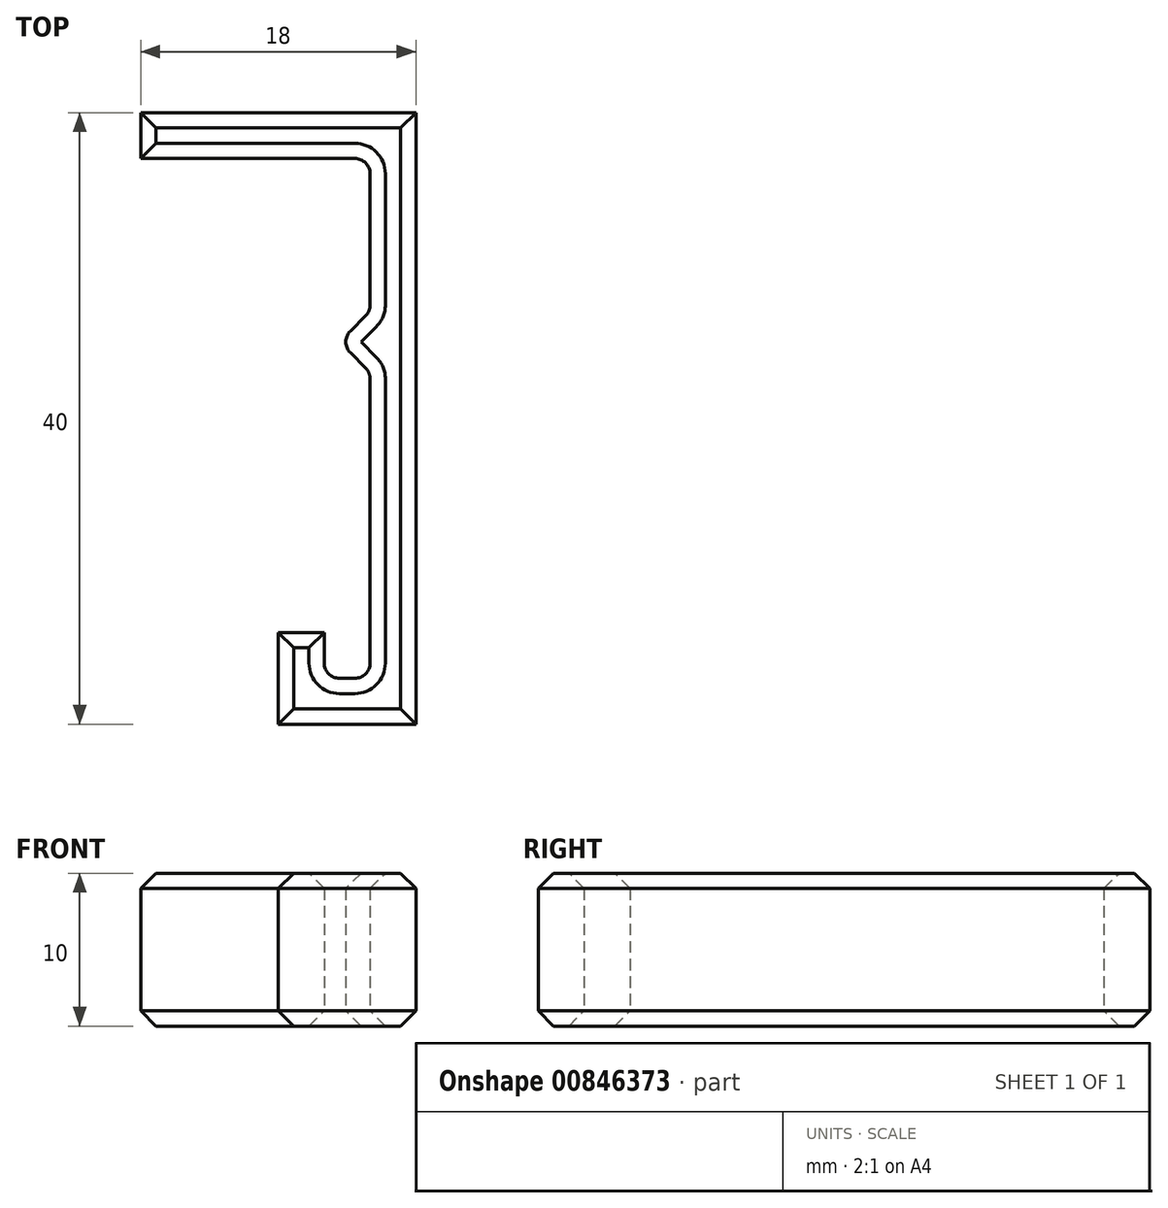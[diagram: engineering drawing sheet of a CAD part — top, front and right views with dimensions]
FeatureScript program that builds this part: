
annotation { "Feature Type Name" : "Feature", "Feature Type Description" : "" }
export const myFeature = defineFeature(function(context is Context, id is Id, definition is map)
    precondition{}
    {
        {
            var Q0;
            Q0=qCreatedBy(makeId("Top.planeOp"),FACE);
            var sketch = newSketch(context, id + "F0", { "sketchPlane" : qUnion([Q0])});
            skLineSegment(sketch, "E0", {"start": v(0, 0) * mm, "end": v(0, -3) * mm});
            skLineSegment(sketch, "E1", {"start": v(0, -3) * mm, "end": v(15, -3) * mm});
            skLineSegment(sketch, "E2", {"start": v(15, -3) * mm, "end": v(15, -13) * mm});
            skLineSegment(sketch, "E3", {"start": v(15, -13) * mm, "end": v(13, -15) * mm});
            skLineSegment(sketch, "E4", {"start": v(13, -15) * mm, "end": v(15, -17) * mm});
            skLineSegment(sketch, "E5", {"start": v(15, -17) * mm, "end": v(15, -37) * mm});
            skLineSegment(sketch, "E6", {"start": v(0, 0) * mm, "end": v(18, 0) * mm});
            skLineSegment(sketch, "E7", {"start": v(18, 0) * mm, "end": v(18, -40) * mm});
            skLineSegment(sketch, "E8", {"start": v(18, -40) * mm, "end": v(9, -40) * mm});
            skLineSegment(sketch, "E9", {"start": v(9, -40) * mm, "end": v(9, -34) * mm});
            skLineSegment(sketch, "E10", {"start": v(9, -34) * mm, "end": v(12, -34) * mm});
            skLineSegment(sketch, "E11", {"start": v(12, -34) * mm, "end": v(12, -37) * mm});
            skLineSegment(sketch, "E12", {"start": v(12, -37) * mm, "end": v(15, -37) * mm});
            skSolve(sketch);
        }
        {
            var Q0;
            Q0 = qSketchRegion(id + "F0", true);
            extrude(context, id + "F1", {"entities" : qUnion([Q0]), "depth" : 10 * mm, "offsetDistance" : 25 * mm});
        }
        {
            var Q0;
            Q0=makeQuery(id+"F1.opExtrude","SWEPT_EDGE",EDGE,{"disambiguationData":[OSD([sQuery(id+"F0.wireOp",EDGE,"E3"),sQuery(id+"F0.wireOp",EDGE,"E4")])]});
            var Q1;
            Q1=makeQuery(id+"F1.opExtrude","SWEPT_EDGE",EDGE,{"disambiguationData":[OSD([sQuery(id+"F0.wireOp",EDGE,"E2"),sQuery(id+"F0.wireOp",EDGE,"E3")])]});
            var Q2;
            Q2=makeQuery(id+"F1.opExtrude","SWEPT_EDGE",EDGE,{"disambiguationData":[OSD([sQuery(id+"F0.wireOp",EDGE,"E5"),sQuery(id+"F0.wireOp",EDGE,"E12")])]});
            var Q3;
            Q3=makeQuery(id+"F1.opExtrude","SWEPT_EDGE",EDGE,{"disambiguationData":[OSD([sQuery(id+"F0.wireOp",EDGE,"E4"),sQuery(id+"F0.wireOp",EDGE,"E5")])]});
            var Q4;
            Q4=makeQuery(id+"F1.opExtrude","SWEPT_EDGE",EDGE,{"disambiguationData":[OSD([sQuery(id+"F0.wireOp",EDGE,"E1"),sQuery(id+"F0.wireOp",EDGE,"E2")])]});
            var Q5;
            Q5=makeQuery(id+"F1.opExtrude","SWEPT_EDGE",EDGE,{"disambiguationData":[OSD([sQuery(id+"F0.wireOp",EDGE,"E11"),sQuery(id+"F0.wireOp",EDGE,"E12")])]});
            fillet(context, id + "F2", {"entities" : qUnion([Q0, Q1, Q2, Q3, Q4, Q5]), "radius" : 1 * mm, "tangentPropagation" : true, "allowEdgeOverflow" : false});
        }
        {
            var Q0;
            Q0=makeQuery(id+"F1.opExtrude","CAP_FACE",FACE,{"disambiguationData":[OSD([sQuery(id+"F0.wireOp",EDGE,"E0"),sQuery(id+"F0.wireOp",EDGE,"E1"),sQuery(id+"F0.wireOp",EDGE,"E2"),sQuery(id+"F0.wireOp",EDGE,"E3"),sQuery(id+"F0.wireOp",EDGE,"E4"),sQuery(id+"F0.wireOp",EDGE,"E5"),sQuery(id+"F0.wireOp",EDGE,"E6"),sQuery(id+"F0.wireOp",EDGE,"E7"),sQuery(id+"F0.wireOp",EDGE,"E8"),sQuery(id+"F0.wireOp",EDGE,"E9"),sQuery(id+"F0.wireOp",EDGE,"E10"),sQuery(id+"F0.wireOp",EDGE,"E11"),sQuery(id+"F0.wireOp",EDGE,"E12")])],"isStart":false});
            var Q1;
            Q1=makeQuery(id+"F1.opExtrude","CAP_FACE",FACE,{"disambiguationData":[OSD([sQuery(id+"F0.wireOp",EDGE,"E0"),sQuery(id+"F0.wireOp",EDGE,"E1"),sQuery(id+"F0.wireOp",EDGE,"E2"),sQuery(id+"F0.wireOp",EDGE,"E3"),sQuery(id+"F0.wireOp",EDGE,"E4"),sQuery(id+"F0.wireOp",EDGE,"E5"),sQuery(id+"F0.wireOp",EDGE,"E6"),sQuery(id+"F0.wireOp",EDGE,"E7"),sQuery(id+"F0.wireOp",EDGE,"E8"),sQuery(id+"F0.wireOp",EDGE,"E9"),sQuery(id+"F0.wireOp",EDGE,"E10"),sQuery(id+"F0.wireOp",EDGE,"E11"),sQuery(id+"F0.wireOp",EDGE,"E12")])],"isStart":true});
            chamfer(context, id + "F3", {"entities" : qUnion([Q0, Q1]), "width" : 1 * mm, "tangentPropagation" : true});
        }
    });
